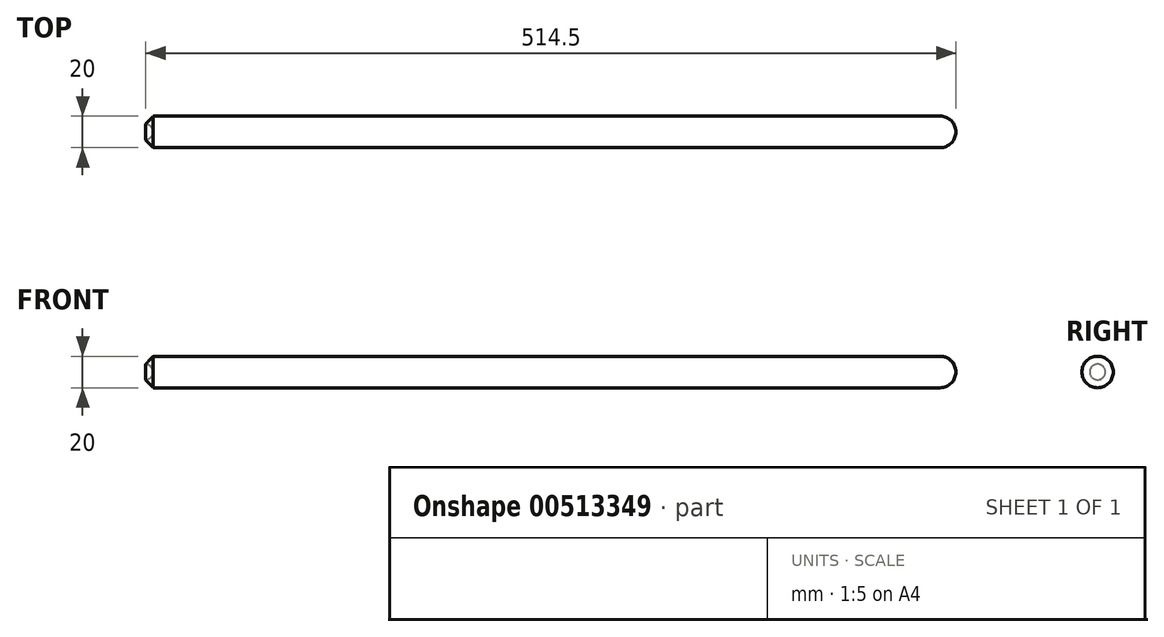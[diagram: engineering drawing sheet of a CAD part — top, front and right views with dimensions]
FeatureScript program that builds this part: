
annotation { "Feature Type Name" : "Feature", "Feature Type Description" : "" }
export const myFeature = defineFeature(function(context is Context, id is Id, definition is map)
    precondition{}
    {
        {
            var Q0;
            Q0=qCreatedBy(makeId("Right.planeOp"),FACE);
            var sketch = newSketch(context, id + "F0", { "sketchPlane" : qUnion([Q0])});
            skCircle(sketch, "E0", {"center": v(0, 0) * mm, "radius": 10 * mm});
            skSolve(sketch);
        }
        {
            var Q0;
            Q0 = qSketchRegion(id + "F0", true);
            extrude(context, id + "F1", {"entities" : qUnion([Q0]), "depth" : 500 * mm});
        }
        {
            var Q0;
            Q0=qCreatedBy(makeId("Front.planeOp"),FACE);
            var sketch = newSketch(context, id + "F2", { "sketchPlane" : qUnion([Q0])});
            skLineSegment(sketch, "E1", {"start": v(0, -9.9) * mm, "end": v(-4.5, -5) * mm});
            skLineSegment(sketch, "E2", {"start": v(-4.5, -5) * mm, "end": v(-4.5, 0) * mm});
            skLineSegment(sketch, "E3", {"start": v(-4.5, 0) * mm, "end": v(0, 0) * mm});
            skLineSegment(sketch, "E4", {"start": v(0, 0) * mm, "end": v(0, -9.9) * mm});
            skSolve(sketch);
        }
        {
            var Q0;
            Q0 = qSketchRegion(id + "F2", true);
            var Q1;
            Q1=sQuery(id+"F2.wireOp",EDGE,"E3");
            revolve(context, id + "F3", {"operationType" : NewBodyOperationType.ADD, "entities" : qUnion([Q0]), "axis" : qUnion([Q1]), "revolveType" : RevolveType.FULL});
        }
        {
            var Q0;
            Q0=qCreatedBy(makeId("Front.planeOp"),FACE);
            var sketch = newSketch(context, id + "F4", { "sketchPlane" : qUnion([Q0])});
            skLineSegment(sketch, "E5", {"start": v(0, 0) * mm, "end": v(-15.42, 0) * mm, "construction": true});
            skArc(sketch, "E6", {"start": v(0, 0) * mm, "mid": v(-1.46, 3.54) * mm, "end": v(-5, 5) * mm});
            skLineSegment(sketch, "E7", {"start": v(-5, 0) * mm, "end": v(-5, 5) * mm});
            skLineSegment(sketch, "E8", {"start": v(-5, 0) * mm, "end": v(0, 0) * mm});
            skSolve(sketch);
        }
        {
            var Q0;
            Q0 = qSketchRegion(id + "F4", true);
            var Q1;
            Q1=sQuery(id+"F4.wireOp",EDGE,"E5");
            revolve(context, id + "F5", {"operationType" : NewBodyOperationType.REMOVE, "entities" : qUnion([Q0]), "axis" : qUnion([Q1]), "revolveType" : RevolveType.FULL, "oppositeDirection" : true});
        }
        {
            var Q0;
            Q0=qCreatedBy(makeId("Front.planeOp"),FACE);
            var sketch = newSketch(context, id + "F6", { "sketchPlane" : qUnion([Q0])});
            skLineSegment(sketch, "E9", {"start": v(500, 0) * mm, "end": v(503.31, 0) * mm, "construction": true});
            skArc(sketch, "E10", {"start": v(510, 0) * mm, "mid": v(507.07, 7.07) * mm, "end": v(500, 10) * mm});
            skLineSegment(sketch, "E11", {"start": v(500, 0) * mm, "end": v(500, 10) * mm});
            skLineSegment(sketch, "E12", {"start": v(500, 0) * mm, "end": v(510, 0) * mm});
            skSolve(sketch);
        }
        {
            var Q0;
            Q0=makeQuery(id+"F6.imprint","IMPRINT",FACE,{"disambiguationData":[TD([[makeQuery(id+"F6.imprint","IMPRINT",EDGE,{"derivedFrom":sQuery(id+"F6.wireOp",EDGE,"E10")}),1.0]])]});
            var Q1;
            Q1=sQuery(id+"F6.wireOp",EDGE,"E12");
            revolve(context, id + "F7", {"operationType" : NewBodyOperationType.ADD, "entities" : qUnion([Q0]), "axis" : qUnion([Q1]), "revolveType" : RevolveType.FULL});
        }
    });
